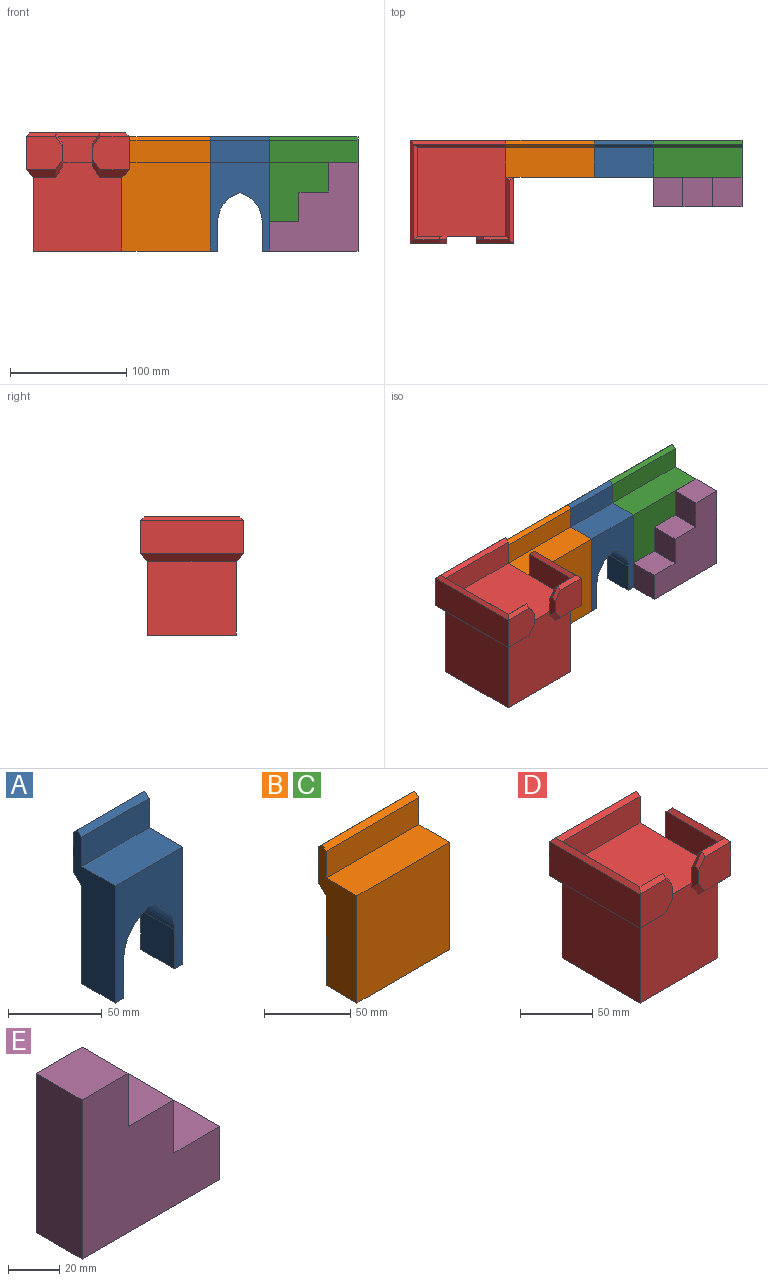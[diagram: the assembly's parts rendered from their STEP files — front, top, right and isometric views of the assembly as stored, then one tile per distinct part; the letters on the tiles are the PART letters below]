
ASSEMBLY  parts=5 mates=8
PART A: 16 faces, bbox 50.8x31.8x98.4 mm
  f0: plane 25.4x6.35mm, normal (0,0,-1), area 161.3mm2, adj f1,f3,f4,f13
  f1: plane 63.5x50.8mm, normal (0,1,0), area 1563.8mm2, adj f0,f2,f4,f6,f9,f12,f13,f14
  f2: plane 98.43x31.75mm, normal (-1,0,0), area 2127mm2, adj f1,f3,f5,f6,f7,f8,f9,f10
  f3: plane 76.2x50.8mm, normal (0,-1,0), area 2209mm2, adj f0,f2,f4,f5,f6,f12,f13,f14
  f4: plane 98.43x31.75mm, normal (1,0,0), area 2127mm2, adj f0,f1,f3,f5,f7,f8,f9,f10
  f5: plane 50.8x25.4mm, normal (0,0,1), area 1290.3mm2, adj f2,f3,f4,f7
  f6: plane 25.4x6.35mm, normal (0,0,-1), area 161.3mm2, adj f1,f2,f3,f12
  f7: plane 50.8x19.05mm, normal (0,-1,0), area 967.7mm2, adj f2,f4,f5,f11
  f8: plane 50.8x25.4mm, normal (0,1,0), area 1290.3mm2, adj f2,f4,f9,f10
  f9: plane 50.8x6.35mm, normal (0,0.71,-0.71), area 456.2mm2, adj f1,f2,f4,f8
  f10: plane 50.8x3.18mm, normal (0,0.71,0.71), area 228.1mm2, adj f2,f4,f8,f11
  f11: plane 50.8x3.18mm, normal (0,-0.71,0.71), area 228.1mm2, adj f2,f4,f7,f10
  f12: plane 25.4x25.4mm, normal (1,0,0), area 645.2mm2, adj f1,f3,f6,f14
  f13: plane 25.4x25.4mm, normal (-1,0,0), area 645.2mm2, adj f0,f1,f3,f15
  f14: cylinder r=25.4mm len=25.4mm, axis (0,1,0), area 850.4mm2, adj f1,f3,f12,f15
  f15: cylinder r=25.4mm len=25.4mm, axis (0,-1,0), area 850.4mm2, adj f1,f3,f13,f14
PART B: 11 faces, bbox 76.2x31.8x98.4 mm
  f0: plane 76.2x63.5mm, normal (0,1,0), area 4838.7mm2, adj f1,f3,f5,f10
  f1: plane 98.43x31.75mm, normal (-1,0,0), area 2127mm2, adj f0,f2,f4,f5,f6,f7,f8,f9
  f2: plane 76.2x76.2mm, normal (0,-1,0), area 5806.4mm2, adj f1,f3,f4,f5
  f3: plane 98.43x31.75mm, normal (1,0,0), area 2127mm2, adj f0,f2,f4,f5,f6,f7,f8,f9
  f4: plane 76.2x25.4mm, normal (0,0,1), area 1935.5mm2, adj f1,f2,f3,f6
  f5: plane 76.2x25.4mm, normal (0,0,-1), area 1935.5mm2, adj f0,f1,f2,f3
  f6: plane 76.2x19.05mm, normal (0,-1,0), area 1451.6mm2, adj f1,f3,f4,f9
  f7: plane 76.2x25.4mm, normal (0,1,0), area 1935.5mm2, adj f1,f3,f8,f10
  f8: plane 76.2x3.18mm, normal (0,0.71,0.71), area 342.1mm2, adj f1,f3,f7,f9
  f9: plane 76.2x3.18mm, normal (0,-0.71,0.71), area 342.1mm2, adj f1,f3,f6,f8
  f10: plane 76.2x6.35mm, normal (0,0.71,-0.71), area 684.3mm2, adj f0,f1,f3,f7
PART C: same geometry as B
PART D: 42 faces, bbox 88.9x88.9x101.6 mm
  f0: plane 25.4x6.35mm, normal (0,-0.71,-0.71), area 199.6mm2, adj f6,f11,f30,f40
  f1: plane 25.4x3.18mm, normal (0,-0.71,0.71), area 106.9mm2, adj f2,f3,f25,f39
  f2: plane 22.23x3.18mm, normal (0,0.71,0.71), area 92.7mm2, adj f1,f4,f26,f38
  f3: plane 31.75x28.58mm, normal (0,-1,0), area 850.2mm2, adj f1,f14,f31,f34,f39,f41
  f4: plane 25.4x22.23mm, normal (0,1,0), area 536mm2, adj f2,f9,f13,f34,f38
  f5: plane 76.2x63.5mm, normal (0,1,0), area 4838.7mm2, adj f7,f8,f10,f33
  f6: plane 76.2x76.2mm, normal (0,-1,0), area 5218.3mm2, adj f0,f7,f8,f9,f10,f31,f34,f35
  f7: plane 76.2x63.5mm, normal (-1,0,0), area 4838.7mm2, adj f5,f6,f10,f32
  f8: plane 101.6x82.55mm, normal (1,0,0), area 5393.1mm2, adj f5,f6,f9,f10,f15,f16,f18,f27
  f9: plane 76.2x76.2mm, normal (0,0,1), area 5806.4mm2, adj f4,f6,f8,f12,f13,f15,f17
  f10: plane 76.2x76.2mm, normal (0,0,-1), area 5806.4mm2, adj f5,f6,f7,f8
  f11: plane 31.75x28.58mm, normal (0,-1,0), area 850.2mm2, adj f0,f19,f23,f35,f36,f40
  f12: plane 25.4x22.23mm, normal (0,1,0), area 536mm2, adj f9,f17,f24,f35,f37
  f13: plane 76.2x22.23mm, normal (1,0,0), area 1693.5mm2, adj f4,f9,f15,f26
  f14: plane 88.9x28.58mm, normal (-1,0,0), area 2540.3mm2, adj f3,f16,f25,f32
  f15: plane 76.2x22.23mm, normal (0,-1,0), area 1693.5mm2, adj f8,f9,f13,f28
  f16: plane 82.55x28.58mm, normal (0,1,0), area 2358.9mm2, adj f8,f14,f27,f33
  f17: plane 50.8x22.23mm, normal (-1,0,0), area 1129mm2, adj f9,f12,f18,f22
  f18: plane 28.58x6.35mm, normal (0,1,0), area 181.5mm2, adj f8,f17,f19,f20,f29
  f19: plane 57.15x28.58mm, normal (1,0,0), area 1633.1mm2, adj f11,f18,f21,f30
  f20: plane 6.35x3.18mm, normal (0,0.71,0.71), area 14.3mm2, adj f18,f21,f22
  f21: plane 57.15x3.18mm, normal (0.71,0,0.71), area 242.4mm2, adj f19,f20,f22,f23
  f22: plane 53.98x3.18mm, normal (-0.71,0,0.71), area 228.1mm2, adj f17,f20,f21,f24
  f23: plane 25.4x3.18mm, normal (0,-0.71,0.71), area 106.9mm2, adj f11,f21,f24,f36
  f24: plane 22.23x3.18mm, normal (0,0.71,0.71), area 92.7mm2, adj f12,f22,f23,f37
  f25: plane 88.9x3.18mm, normal (-0.71,0,0.71), area 384.9mm2, adj f1,f14,f26,f27
  f26: plane 82.55x3.18mm, normal (0.71,0,0.71), area 356.4mm2, adj f2,f13,f25,f28
  f27: plane 82.55x3.18mm, normal (0,0.71,0.71), area 363.5mm2, adj f8,f16,f25,f28
  f28: plane 79.38x3.18mm, normal (0,-0.71,0.71), area 349.3mm2, adj f8,f15,f26,f27
  f29: plane 6.35x6.35mm, normal (0,0.71,-0.71), area 28.5mm2, adj f8,f18,f30
  f30: plane 57.15x6.35mm, normal (0.71,0,-0.71), area 456.2mm2, adj f0,f8,f19,f29
  f31: plane 25.4x6.35mm, normal (0,-0.71,-0.71), area 199.6mm2, adj f3,f6,f32,f41
  f32: plane 88.9x6.35mm, normal (-0.71,0,-0.71), area 741.3mm2, adj f7,f14,f31,f33
  f33: plane 82.55x6.35mm, normal (0,0.71,-0.71), area 712.8mm2, adj f5,f8,f16,f32
  f34: plane 20.14x6.35mm, normal (1,0,0), area 97.6mm2, adj f3,f4,f6,f38,f39,f41
  f35: plane 20.14x6.35mm, normal (-1,0,0), area 97.6mm2, adj f6,f11,f12,f36,f37,f40
  f36: plane 12.16x6.35mm, normal (-0.71,-0.5,0.5), area 40.3mm2, adj f11,f23,f35,f37
  f37: plane 12.16x6.35mm, normal (-0.71,0.5,0.5), area 40.3mm2, adj f12,f24,f35,f36
  f38: plane 12.16x6.35mm, normal (0.71,0.5,0.5), area 40.3mm2, adj f2,f4,f34,f39
  f39: plane 12.16x6.35mm, normal (0.71,-0.5,0.5), area 40.3mm2, adj f1,f3,f34,f38
  f40: plane 15.33x6.35mm, normal (-0.71,-0.5,-0.5), area 80.6mm2, adj f0,f6,f11,f35
  f41: plane 15.33x6.35mm, normal (0.71,-0.5,-0.5), area 80.6mm2, adj f3,f6,f31,f34
PART E: 10 faces, bbox 76.2x25.4x76.2 mm
  f0: plane 76.2x76.2mm, normal (0,1,0), area 3871mm2, adj f2,f3,f4,f5,f6,f7,f8,f9
  f1: plane 76.2x76.2mm, normal (0,-1,0), area 3871mm2, adj f2,f3,f4,f5,f6,f7,f8,f9
  f2: plane 25.4x25.4mm, normal (1,0,0), area 645.2mm2, adj f0,f1,f3,f4
  f3: plane 25.4x25.4mm, normal (0,0,1), area 645.2mm2, adj f0,f1,f2,f5
  f4: plane 76.2x25.4mm, normal (0,0,-1), area 1935.5mm2, adj f0,f1,f2,f8
  f5: plane 25.4x25.4mm, normal (1,0,0), area 645.2mm2, adj f0,f1,f3,f6
  f6: plane 25.4x25.4mm, normal (0,0,1), area 645.2mm2, adj f0,f1,f5,f7
  f7: plane 25.4x25.4mm, normal (1,0,0), area 645.2mm2, adj f0,f1,f6,f9
  f8: plane 76.2x25.4mm, normal (-1,0,0), area 1935.5mm2, adj f0,f1,f4,f9
  f9: plane 25.4x25.4mm, normal (0,0,1), area 645.2mm2, adj f0,f1,f7,f8
PLACE A rot(axis=(-1,0,0.05),0deg) t=(-3.41,76.2,-49.84)mm
PLACE B rot(axis=(-1,0,0),0deg) t=(-66.91,76.2,-49.84)mm
PLACE C rot(axis=(1,0,0),0deg) t=(60.09,76.2,-49.84)mm
PLACE D rot(axis=(-1,0,0),0deg) t=(-143.11,50.8,-49.84)mm
PLACE E rot(axis=(0,0,-1),180deg) t=(60.09,50.8,-49.84)mm
MATE planar B.f0 <-> C.f0  axis (0,1,0) through (-66.91,88.9,-18.09)mm
MATE planar E.f4 <-> C.f5  axis (0,0,-1) through (60.09,50.8,-49.84)mm
MATE planar A.f0 <-> C.f5  axis (0,0,-1) through (18.81,76.2,-49.84)mm
MATE planar B.f0 <-> D.f5  axis (0,1,0) through (-66.91,88.9,-18.09)mm
MATE planar B.f5 <-> A.f6  axis (0,0,-1) through (-66.91,76.2,-49.84)mm
MATE planar E.f8 <-> C.f3  axis (1,0,0) through (98.19,50.8,-11.74)mm
MATE planar D.f10 <-> B.f5  axis (0,0,-1) through (-105.01,50.8,-49.84)mm
MATE planar A.f1 <-> B.f0  axis (0,1,0) through (-3.41,88.9,13.66)mm
